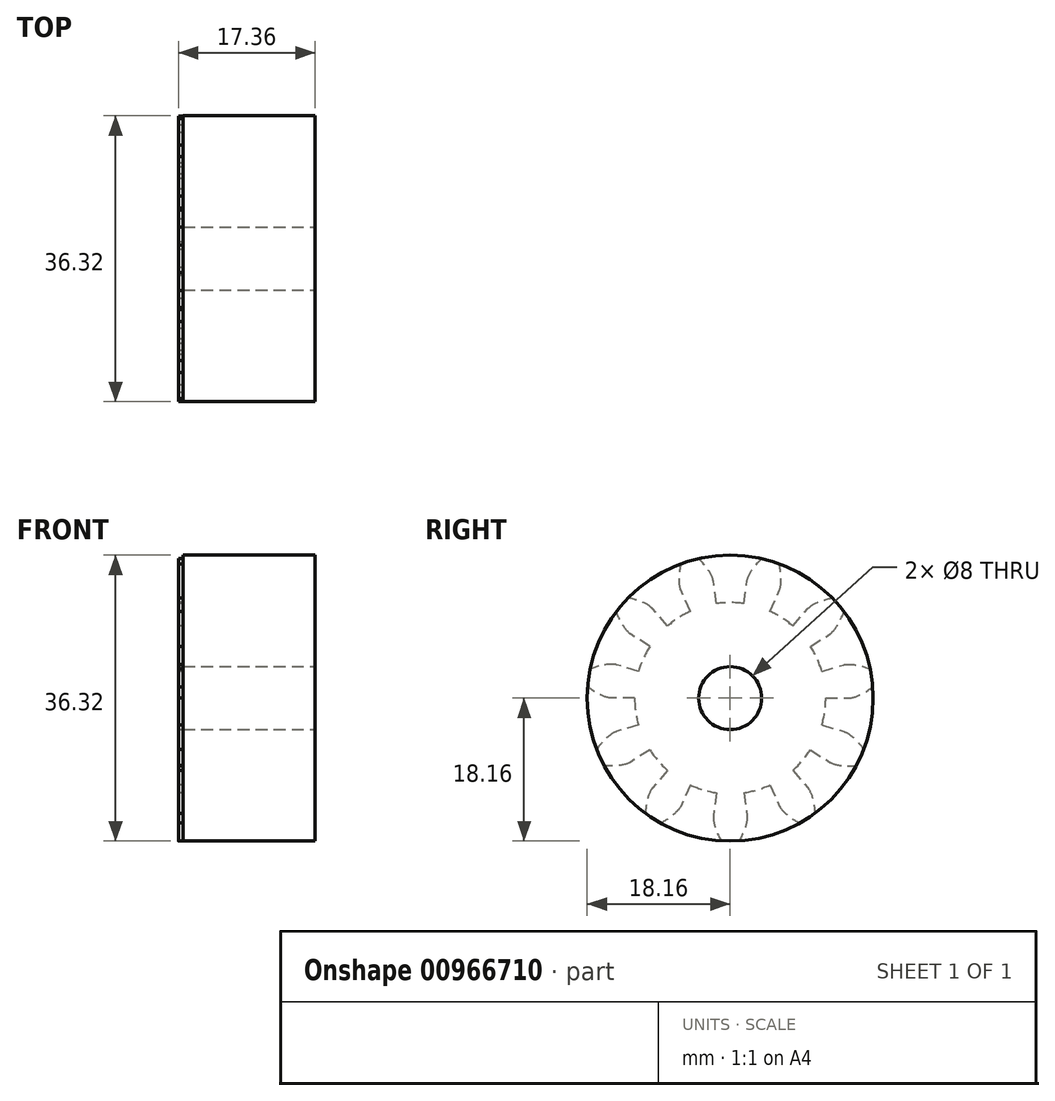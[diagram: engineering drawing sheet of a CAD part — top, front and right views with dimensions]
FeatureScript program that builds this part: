
annotation { "Feature Type Name" : "Feature", "Feature Type Description" : "" }
export const myFeature = defineFeature(function(context is Context, id is Id, definition is map)
    precondition{}
    {
        {
            assignVariable(context, id + "F0", {"name" : "NumberTeeth", "anyValue" : 11});
        }
        {
            assignVariable(context, id + "F1", {"name" : "GearThickness", "anyValue" : .6});
        }
        {
            var Q0;
            Q0=qCreatedBy(makeId("Right.planeOp"),FACE);
            var sketch = newSketch(context, id + "F2", { "sketchPlane" : qUnion([Q0])});
            skCircle(sketch, "E0", {"center": v(0, 0) * mm, "radius": 12.14 * mm});
            skCircle(sketch, "E1", {"center": v(0, 0) * mm, "radius": 15.09 * mm, "construction": true});
            skCircle(sketch, "E2", {"center": v(0, 0) * mm, "radius": 15.37 * mm, "construction": true});
            skCircle(sketch, "E3", {"center": v(0, 0) * mm, "radius": 18.16 * mm});
            skLineSegment(sketch, "E4", {"start": v(0, 0) * mm, "end": v(-15.09, 0) * mm, "construction": true});
            skLineSegment(sketch, "E5.1.0", {"start": v(0, 0) * mm, "end": v(-15.07, 0.75) * mm, "construction": true});
            skLineSegment(sketch, "E5.2.0", {"start": v(0, 0) * mm, "end": v(-15.01, 1.5) * mm, "construction": true});
            skLineSegment(sketch, "E5.3.0", {"start": v(0, 0) * mm, "end": v(-14.92, 2.25) * mm, "construction": true});
            skLineSegment(sketch, "E5.4.0", {"start": v(0, 0) * mm, "end": v(-14.79, 3) * mm, "construction": true});
            skLineSegment(sketch, "E5.5.0", {"start": v(0, 0) * mm, "end": v(-14.62, 3.73) * mm, "construction": true});
            skLineSegment(sketch, "E5.6.0", {"start": v(0, 0) * mm, "end": v(-14.41, 4.46) * mm, "construction": true});
            skLineSegment(sketch, "E5.7.0", {"start": v(0, 0) * mm, "end": v(-14.17, 5.17) * mm, "construction": true});
            skLineSegment(sketch, "E5.8.0", {"start": v(0, 0) * mm, "end": v(-13.9, 5.87) * mm, "construction": true});
            skLineSegment(sketch, "E5.9.0", {"start": v(0, 0) * mm, "end": v(-13.58, 6.56) * mm, "construction": true});
            skLineSegment(sketch, "E5.10.0", {"start": v(0, 0) * mm, "end": v(-13.24, 7.23) * mm, "construction": true});
            skLineSegment(sketch, "E5.11.0", {"start": v(0, 0) * mm, "end": v(-12.86, 7.89) * mm, "construction": true});
            skLineSegment(sketch, "E5.12.0", {"start": v(0, 0) * mm, "end": v(-12.45, 8.52) * mm, "construction": true});
            skLineSegment(sketch, "E5.13.0", {"start": v(0, 0) * mm, "end": v(-12, 9.13) * mm, "construction": true});
            skLineSegment(sketch, "E5.14.0", {"start": v(0, 0) * mm, "end": v(-11.54, 9.72) * mm, "construction": true});
            skLineSegment(sketch, "E5.anchor2", {"start": v(0, 0) * mm, "end": v(-11.54, 9.72) * mm, "construction": true});
            skLineSegment(sketch, "E6", {"start": v(-15.07, 0.75) * mm, "end": v(-15.1, 0) * mm, "construction": true});
            skLineSegment(sketch, "E7", {"start": v(-15.01, 1.5) * mm, "end": v(-15.16, 0) * mm, "construction": true});
            skLineSegment(sketch, "E8", {"start": v(-14.92, 2.25) * mm, "end": v(-15.25, 0.02) * mm, "construction": true});
            skLineSegment(sketch, "E9", {"start": v(-14.62, 3.73) * mm, "end": v(-15.55, 0.08) * mm, "construction": true});
            skLineSegment(sketch, "E10", {"start": v(-14.41, 4.46) * mm, "end": v(-15.75, 0.13) * mm, "construction": true});
            skLineSegment(sketch, "E11", {"start": v(-14.17, 5.17) * mm, "end": v(-15.98, 0.21) * mm, "construction": true});
            skLineSegment(sketch, "E12", {"start": v(-13.9, 5.87) * mm, "end": v(-16.25, 0.32) * mm, "construction": true});
            skLineSegment(sketch, "E13", {"start": v(-13.58, 6.56) * mm, "end": v(-16.54, 0.45) * mm, "construction": true});
            skLineSegment(sketch, "E14", {"start": v(-13.24, 7.23) * mm, "end": v(-16.86, 0.61) * mm, "construction": true});
            skLineSegment(sketch, "E15", {"start": v(-12.86, 7.89) * mm, "end": v(-17.2, 0.81) * mm, "construction": true});
            skLineSegment(sketch, "E16", {"start": v(-14.79, 3) * mm, "end": v(-15.38, 0.04) * mm, "construction": true});
            skLineSegment(sketch, "E17", {"start": v(-12.45, 8.52) * mm, "end": v(-17.56, 1.05) * mm, "construction": true});
            skLineSegment(sketch, "E18", {"start": v(-12, 9.13) * mm, "end": v(-17.94, 1.32) * mm, "construction": true});
            skLineSegment(sketch, "E19", {"start": v(-11.54, 9.72) * mm, "end": v(-18.34, 1.64) * mm, "construction": true});
            skLineSegment(sketch, "E20", {"start": v(0, 0) * mm, "end": v(-14.93, 2.15) * mm, "construction": true});
            skLineSegment(sketch, "E21", {"start": v(-12.14, 0) * mm, "end": v(-15.09, 0) * mm});
            skLineSegment(sketch, "E22.MirrorCS", {"start": v(-11.64, 3.42) * mm, "end": v(-14.48, 4.25) * mm});
            skFitSpline(sketch, "E23", {"points": [v(-15.09, 0) * mm, v(-15.1, 0) * mm, v(-15.16, 0) * mm, v(-15.25, 0.02) * mm, v(-15.38, 0.04) * mm, v(-15.55, 0.08) * mm, v(-15.75, 0.13) * mm, v(-15.98, 0.21) * mm, v(-16.25, 0.32) * mm, v(-16.54, 0.45) * mm, v(-16.86, 0.61) * mm, v(-17.2, 0.81) * mm, v(-17.56, 1.05) * mm, v(-17.94, 1.32) * mm, v(-18.34, 1.64) * mm], "startDerivative": vector(-0.82, 0) * mm, "endDerivative": vector(-1.2, 1) * mm});
            skLineSegment(sketch, "E24", {"start": v(-18.34, 1.64) * mm, "end": v(-18.91, 2.12) * mm, "construction": true});
            skFitSpline(sketch, "E25.MirrorCS", {"points": [v(-14.48, 4.25) * mm, v(-14.5, 4.25) * mm, v(-14.55, 4.27) * mm, v(-14.64, 4.28) * mm, v(-14.77, 4.3) * mm, v(-14.94, 4.3) * mm, v(-15.15, 4.3) * mm, v(-15.4, 4.3) * mm, v(-15.68, 4.27) * mm, v(-16, 4.23) * mm, v(-16.35, 4.16) * mm, v(-16.73, 4.07) * mm, v(-17.15, 3.94) * mm, v(-17.6, 3.79) * mm, v(-18.06, 3.6) * mm], "startDerivative": vector(-0.78, 0.23) * mm, "endDerivative": vector(-1.42, -0.63) * mm});
            skSolve(sketch);
        }
        {
            var Q0;
            {var subQ0=sQuery(id+"F2.wireOp",EDGE,"E0");var subQ27=makeQuery(id+"F2.imprint","INTERSECT",VERTEX,{"derivedFrom":[subQ0,sQuery(id+"F2.wireOp",EDGE,"10ea1024-8cf5-41f5-a75f-a634b86921f3.10.0")]});Q0=makeQuery(id+"F2.imprint","IMPRINT",FACE,{"disambiguationData":[TD([[makeQuery(id+"F2.imprint","IMPRINT",EDGE,{"disambiguationData":[TD([[subQ27,-1.0]])],"derivedFrom":subQ0}),1.0]])]});}
            var Q1;
            {var subQ0=sQuery(id+"F2.wireOp",EDGE,"10ea1024-8cf5-41f5-a75f-a634b86921f3.1.0");Q1=makeQuery(id+"F2.imprint","IMPRINT",FACE,{"disambiguationData":[TD([[makeQuery(id+"F2.imprint","IMPRINT",EDGE,{"derivedFrom":subQ0}),-1.0]])]});}
            var Q2;
            {var subQ7=sQuery(id+"F2.wireOp",EDGE,"10ea1024-8cf5-41f5-a75f-a634b86921f3.2.0");Q2=makeQuery(id+"F2.imprint","IMPRINT",FACE,{"disambiguationData":[TD([[makeQuery(id+"F2.imprint","IMPRINT",EDGE,{"derivedFrom":subQ7}),-1.0]])]});}
            var Q3;
            {var subQ8=sQuery(id+"F2.wireOp",EDGE,"10ea1024-8cf5-41f5-a75f-a634b86921f3.3.0");Q3=makeQuery(id+"F2.imprint","IMPRINT",FACE,{"disambiguationData":[TD([[makeQuery(id+"F2.imprint","IMPRINT",EDGE,{"derivedFrom":subQ8}),-1.0]])]});}
            var Q4;
            {var subQ2=sQuery(id+"F2.wireOp",EDGE,"10ea1024-8cf5-41f5-a75f-a634b86921f3.4.0");Q4=makeQuery(id+"F2.imprint","IMPRINT",FACE,{"disambiguationData":[TD([[makeQuery(id+"F2.imprint","IMPRINT",EDGE,{"derivedFrom":subQ2}),-1.0]])]});}
            var Q5;
            {var subQ8=sQuery(id+"F2.wireOp",EDGE,"10ea1024-8cf5-41f5-a75f-a634b86921f3.5.0");Q5=makeQuery(id+"F2.imprint","IMPRINT",FACE,{"disambiguationData":[TD([[makeQuery(id+"F2.imprint","IMPRINT",EDGE,{"derivedFrom":subQ8}),-1.0]])]});}
            var Q6;
            {var subQ3=sQuery(id+"F2.wireOp",EDGE,"10ea1024-8cf5-41f5-a75f-a634b86921f3.6.0");Q6=makeQuery(id+"F2.imprint","IMPRINT",FACE,{"disambiguationData":[TD([[makeQuery(id+"F2.imprint","IMPRINT",EDGE,{"derivedFrom":subQ3}),-1.0]])]});}
            var Q7;
            {var subQ0=sQuery(id+"F2.wireOp",EDGE,"10ea1024-8cf5-41f5-a75f-a634b86921f3.7.0");Q7=makeQuery(id+"F2.imprint","IMPRINT",FACE,{"disambiguationData":[TD([[makeQuery(id+"F2.imprint","IMPRINT",EDGE,{"derivedFrom":subQ0}),-1.0]])]});}
            var Q8;
            {var subQ5=sQuery(id+"F2.wireOp",EDGE,"10ea1024-8cf5-41f5-a75f-a634b86921f3.8.0");Q8=makeQuery(id+"F2.imprint","IMPRINT",FACE,{"disambiguationData":[TD([[makeQuery(id+"F2.imprint","IMPRINT",EDGE,{"derivedFrom":subQ5}),-1.0]])]});}
            var Q9;
            {var subQ1=sQuery(id+"F2.wireOp",EDGE,"10ea1024-8cf5-41f5-a75f-a634b86921f3.9.0");Q9=makeQuery(id+"F2.imprint","IMPRINT",FACE,{"disambiguationData":[TD([[makeQuery(id+"F2.imprint","IMPRINT",EDGE,{"derivedFrom":subQ1}),-1.0]])]});}
            var Q10;
            {var subQ5=sQuery(id+"F2.wireOp",EDGE,"10ea1024-8cf5-41f5-a75f-a634b86921f3.10.0");Q10=makeQuery(id+"F2.imprint","IMPRINT",FACE,{"disambiguationData":[TD([[makeQuery(id+"F2.imprint","IMPRINT",EDGE,{"derivedFrom":subQ5}),-1.0]])]});}
            var Q11;
            {var subQ8=sQuery(id+"F2.wireOp",EDGE,"10ea1024-8cf5-41f5-a75f-a634b86921f3.11.0");Q11=makeQuery(id+"F2.imprint","IMPRINT",FACE,{"disambiguationData":[TD([[makeQuery(id+"F2.imprint","IMPRINT",EDGE,{"derivedFrom":subQ8}),-1.0]])]});}
            var Q12;
            {var subQ2=sQuery(id+"F2.wireOp",EDGE,"10ea1024-8cf5-41f5-a75f-a634b86921f3.12.0");Q12=makeQuery(id+"F2.imprint","IMPRINT",FACE,{"disambiguationData":[TD([[makeQuery(id+"F2.imprint","IMPRINT",EDGE,{"derivedFrom":subQ2}),-1.0]])]});}
            var Q13;
            {var subQ3=sQuery(id+"F2.wireOp",EDGE,"10ea1024-8cf5-41f5-a75f-a634b86921f3.13.0");Q13=makeQuery(id+"F2.imprint","IMPRINT",FACE,{"disambiguationData":[TD([[makeQuery(id+"F2.imprint","IMPRINT",EDGE,{"derivedFrom":subQ3}),-1.0]])]});}
            var Q14;
            {var subQ0=sQuery(id+"F2.wireOp",EDGE,"10ea1024-8cf5-41f5-a75f-a634b86921f3.14.0");Q14=makeQuery(id+"F2.imprint","IMPRINT",FACE,{"disambiguationData":[TD([[makeQuery(id+"F2.imprint","IMPRINT",EDGE,{"derivedFrom":subQ0}),-1.0]])]});}
            var Q15;
            {var subQ6=sQuery(id+"F2.wireOp",EDGE,"10ea1024-8cf5-41f5-a75f-a634b86921f3.15.0");Q15=makeQuery(id+"F2.imprint","IMPRINT",FACE,{"disambiguationData":[TD([[makeQuery(id+"F2.imprint","IMPRINT",EDGE,{"derivedFrom":subQ6}),-1.0]])]});}
            var Q16;
            {var subQ5=sQuery(id+"F2.wireOp",EDGE,"10ea1024-8cf5-41f5-a75f-a634b86921f3.16.0");Q16=makeQuery(id+"F2.imprint","IMPRINT",FACE,{"disambiguationData":[TD([[makeQuery(id+"F2.imprint","IMPRINT",EDGE,{"derivedFrom":subQ5}),-1.0]])]});}
            var Q17;
            {var subQ7=sQuery(id+"F2.wireOp",EDGE,"10ea1024-8cf5-41f5-a75f-a634b86921f3.17.0");Q17=makeQuery(id+"F2.imprint","IMPRINT",FACE,{"disambiguationData":[TD([[makeQuery(id+"F2.imprint","IMPRINT",EDGE,{"derivedFrom":subQ7}),-1.0]])]});}
            var Q18;
            {var subQ5=sQuery(id+"F2.wireOp",EDGE,"10ea1024-8cf5-41f5-a75f-a634b86921f3.18.0");Q18=makeQuery(id+"F2.imprint","IMPRINT",FACE,{"disambiguationData":[TD([[makeQuery(id+"F2.imprint","IMPRINT",EDGE,{"derivedFrom":subQ5}),-1.0]])]});}
            var Q19;
            {var subQ8=sQuery(id+"F2.wireOp",EDGE,"10ea1024-8cf5-41f5-a75f-a634b86921f3.19.0");Q19=makeQuery(id+"F2.imprint","IMPRINT",FACE,{"disambiguationData":[TD([[makeQuery(id+"F2.imprint","IMPRINT",EDGE,{"derivedFrom":subQ8}),-1.0]])]});}
            var Q20;
            {var subQ8=sQuery(id+"F2.wireOp",EDGE,"E21");Q20=makeQuery(id+"F2.imprint","IMPRINT",FACE,{"disambiguationData":[TD([[makeQuery(id+"F2.imprint","IMPRINT",EDGE,{"derivedFrom":subQ8}),-1.0]])]});}
            extrude(context, id + "F3", {"entities" : qUnion([Q0, Q1, Q2, Q3, Q4, Q5, Q6, Q7, Q8, Q9, Q10, Q11, Q12, Q13, Q14, Q15, Q16, Q17, Q18, Q19, Q20]), "depth" : (getVariable(context, 'GearThickness')) * mm});
        }
        {
            var Q0;
            Q0=makeQuery(id+"F3.opExtrude","SWEPT_FACE",FACE,{"disambiguationData":[OSD([sQuery(id+"F2.wireOp",EDGE,"E25.MirrorCS")])]});
            var Q1;
            Q1=makeQuery(id+"F3.opExtrude","SWEPT_FACE",FACE,{"disambiguationData":[OSD([sQuery(id+"F2.wireOp",EDGE,"E23")])]});
            var Q2;
            Q2=makeQuery(id+"F3.opExtrude","SWEPT_FACE",FACE,{"disambiguationData":[OSD([sQuery(id+"F2.wireOp",EDGE,"E3")])]});
            var Q3;
            Q3=makeQuery(id+"F3.opExtrude","SWEPT_FACE",FACE,{"disambiguationData":[OSD([sQuery(id+"F2.wireOp",EDGE,"E22.MirrorCS")])]});
            var Q4;
            Q4=makeQuery(id+"F3.opExtrude","SWEPT_FACE",FACE,{"disambiguationData":[OSD([sQuery(id+"F2.wireOp",EDGE,"E21")])]});
            var Q5;
            Q5=makeQuery(id+"F3.opExtrude","SWEPT_FACE",FACE,{"disambiguationData":[OSD([sQuery(id+"F2.wireOp",EDGE,"E0")])]});
            circularPattern(context, id + "F4", {"faces" : qUnion([Q0, Q1, Q2, Q3, Q4]), "axis" : qUnion([Q5]), "angle" : 360 * degree, "instanceCount" : getVariable(context, 'NumberTeeth'), "equalSpace" : true, "patternType" : PatternType.FACE});
        }
        {
            var Q0;
            Q0=qCreatedBy(makeId("Top.planeOp"),FACE);
            var sketch = newSketch(context, id + "F5", { "sketchPlane" : qUnion([Q0])});
            skLineSegment(sketch, "E26", {"start": v(0, 0) * mm, "end": v(15.24, 0) * mm, "construction": true});
            skLineSegment(sketch, "E27", {"start": v(15.24, 0) * mm, "end": v(32, 0) * mm, "construction": true});
            skPoint(sketch, "E28", {"position": v(15.24, 0) * mm});
            skPoint(sketch, "E29", {"position": v(32, 0) * mm});
            skSolve(sketch);
        }
        {
            var Q0;
            Q0=makeQuery(id+"F3.opExtrude","CAP_FACE",FACE,{"disambiguationData":[OSD([sQuery(id+"F2.wireOp",EDGE,"E0"),sQuery(id+"F2.wireOp",EDGE,"E3"),sQuery(id+"F2.wireOp",EDGE,"E21"),sQuery(id+"F2.wireOp",EDGE,"E22.MirrorCS"),sQuery(id+"F2.wireOp",EDGE,"E23"),sQuery(id+"F2.wireOp",EDGE,"E25.MirrorCS")])],"isStart":false});
            cPlane(context, id + "F6", {"entities" : qUnion([Q0]), "cplaneType" : CPlaneType.OFFSET, "offset" : 0 * mm, "width" : 152.4 * mm, "height" : 152.4 * mm});
        }
        {
            var Q0;
            Q0=qCreatedBy(id+"F6.planeOp",FACE);
            var sketch = newSketch(context, id + "F7", { "sketchPlane" : qUnion([Q0])});
            skPoint(sketch, "E30.0", {"position": v(0, 0) * mm});
            skCircle(sketch, "E31", {"center": v(0, 0) * mm, "radius": 18.16 * mm});
            skSolve(sketch);
        }
        {
            var Q0;
            Q0=makeQuery(id+"F7.imprint","IMPRINT",FACE,{"disambiguationData":[TD([[makeQuery(id+"F7.imprint","IMPRINT",EDGE,{"derivedFrom":sQuery(id+"F7.wireOp",EDGE,"E31")}),1.0]])]});
            extrude(context, id + "F8", {"entities" : qUnion([Q0]), "depth" : 16.76 * mm, "offsetDistance" : 25.4 * mm});
        }
        {
            var Q0;
            Q0=qCreatedBy(id+"F6.planeOp",FACE);
            var sketch = newSketch(context, id + "F9", { "sketchPlane" : qUnion([Q0])});
            skCircle(sketch, "E32", {"center": v(0, 0) * mm, "radius": 4 * mm});
            skSolve(sketch);
        }
        {
            var Q0;
            Q0 = qSketchRegion(id + "F9", true);
            extrude(context, id + "F10", {"entities" : qUnion([Q0]), "operationType" : NewBodyOperationType.REMOVE, "endBound" : BoundingType.THROUGH_ALL, "oppositeDirection" : true, "depth" : 25.4 * mm, "offsetDistance" : 25.4 * mm, "hasSecondDirection" : true, "secondDirectionBound" : SecondDirectionBoundingType.THROUGH_ALL, "secondDirectionOppositeDirection" : false, "secondDirectionDepth" : 25.4 * mm});
        }
    });
